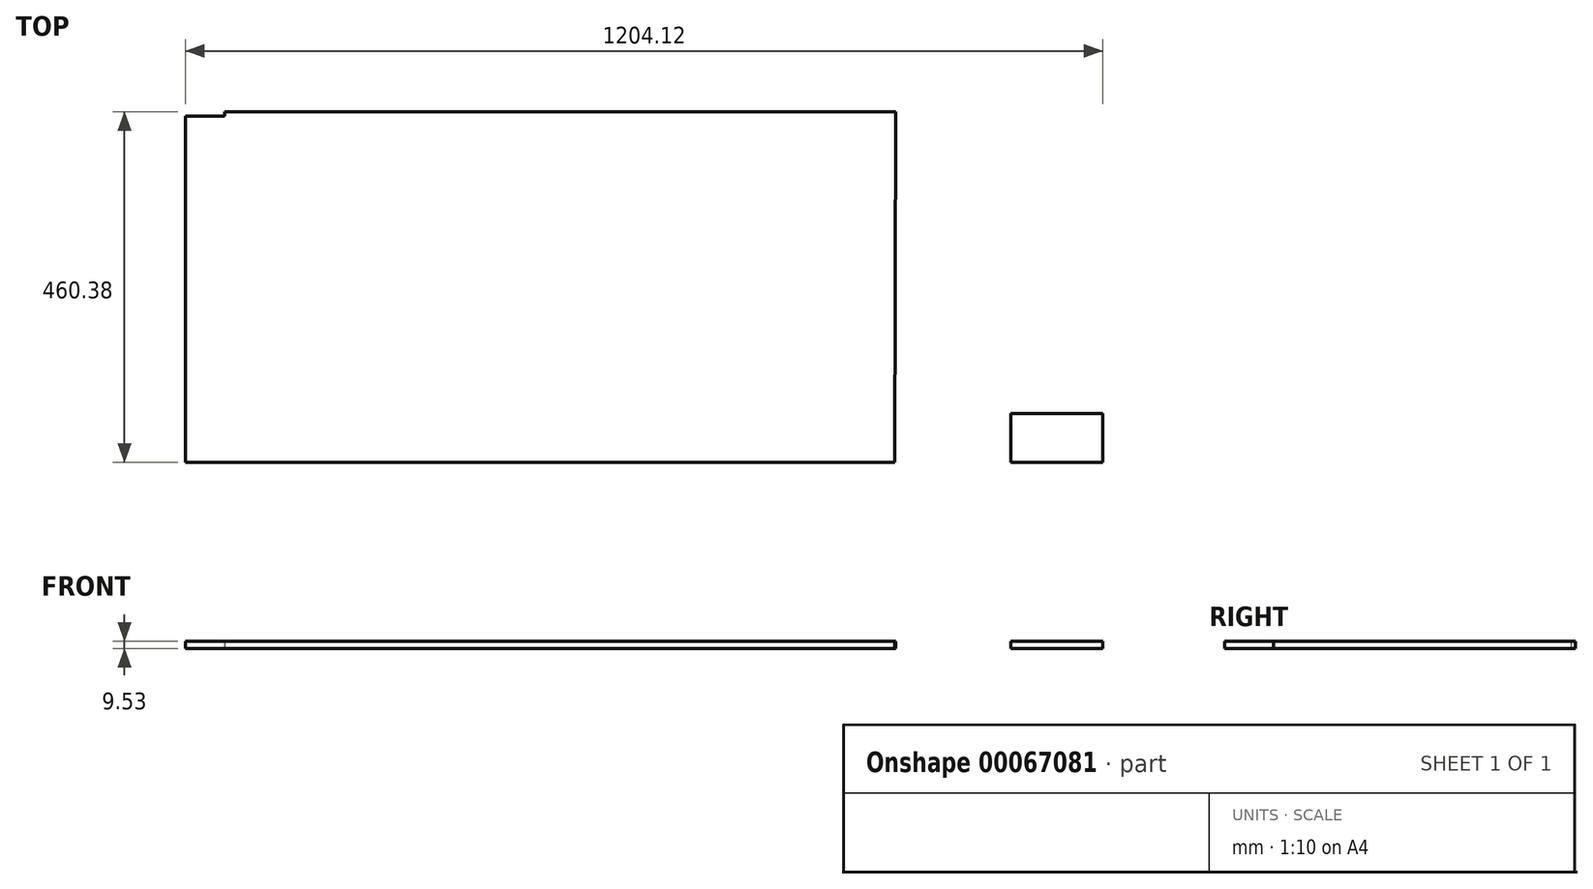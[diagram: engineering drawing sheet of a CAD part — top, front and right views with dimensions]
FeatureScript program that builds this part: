
annotation { "Feature Type Name" : "Feature", "Feature Type Description" : "" }
export const myFeature = defineFeature(function(context is Context, id is Id, definition is map)
    precondition{}
    {
        {
            var Q0;
            Q0=qCreatedBy(makeId("Top.planeOp"),FACE);
            var sketch = newSketch(context, id + "F0", { "sketchPlane" : qUnion([Q0])});
            skLineSegment(sketch, "E0", {"start": v(0, 0) * mm, "end": v(0, 454.82) * mm});
            skLineSegment(sketch, "E1", {"start": v(0, 454.82) * mm, "end": v(51.6, 454.82) * mm});
            skLineSegment(sketch, "E2", {"start": v(51.6, 454.82) * mm, "end": v(51.6, 460.38) * mm});
            skLineSegment(sketch, "E3", {"start": v(51.6, 460.38) * mm, "end": v(932.26, 460.38) * mm});
            skLineSegment(sketch, "E4", {"start": v(932.26, 460.38) * mm, "end": v(931.07, 0) * mm});
            skLineSegment(sketch, "E5", {"start": v(931.07, 0) * mm, "end": v(0, 0) * mm});
            skLineSegment(sketch, "E6.bottom", {"start": v(1083.47, 0) * mm, "end": v(1204.12, 0) * mm});
            skLineSegment(sketch, "E6.top", {"start": v(1083.47, 64.3) * mm, "end": v(1204.12, 64.3) * mm});
            skLineSegment(sketch, "E6.left", {"start": v(1083.47, 0) * mm, "end": v(1083.47, 64.3) * mm});
            skLineSegment(sketch, "E6.right", {"start": v(1204.12, 0) * mm, "end": v(1204.12, 64.3) * mm});
            skSolve(sketch);
        }
        {
            var Q0;
            Q0 = qSketchRegion(id + "F0", true);
            extrude(context, id + "F1", {"entities" : qUnion([Q0]), "depth" : 9.52 * mm});
        }
    });
